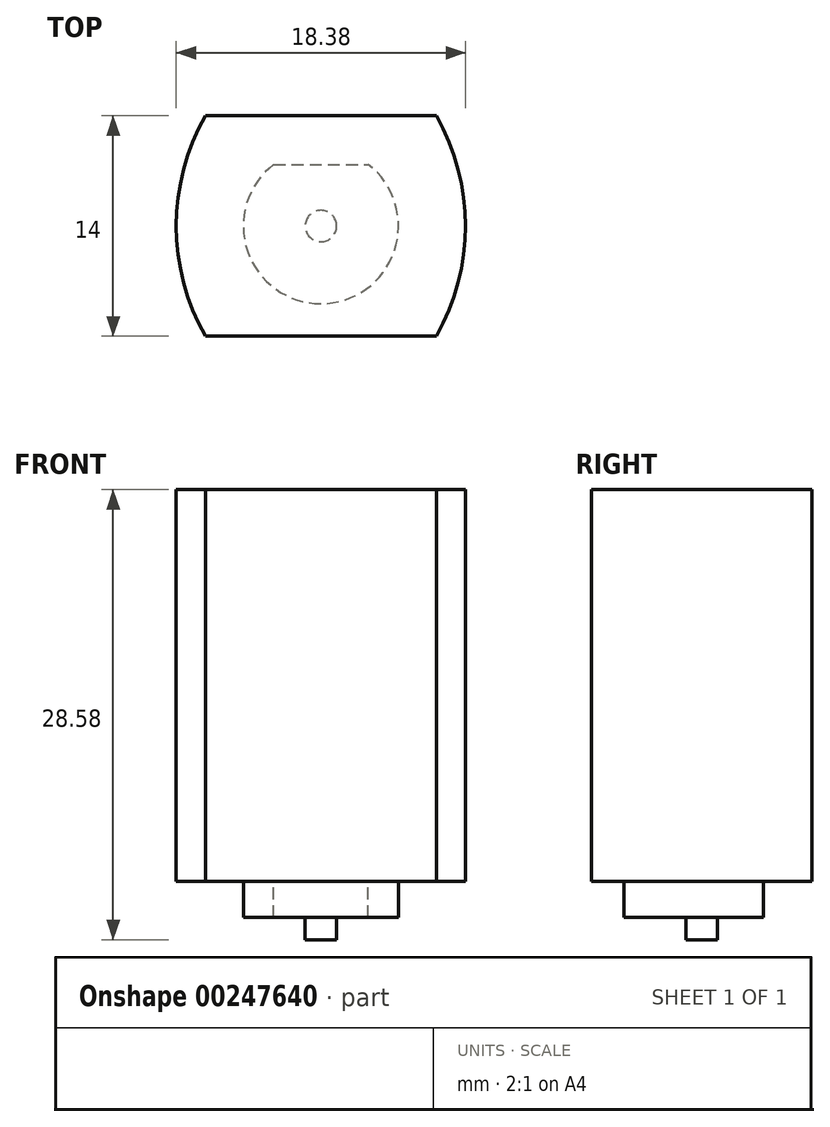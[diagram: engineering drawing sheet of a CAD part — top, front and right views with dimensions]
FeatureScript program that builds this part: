
annotation { "Feature Type Name" : "Feature", "Feature Type Description" : "" }
export const myFeature = defineFeature(function(context is Context, id is Id, definition is map)
    precondition{}
    {
        {
            var Q0;
            Q0=qCreatedBy(makeId("Top.planeOp"),FACE);
            var sketch = newSketch(context, id + "F0", { "sketchPlane" : qUnion([Q0])});
            skLineSegment(sketch, "E0.bottom", {"start": v(9.19, -7) * mm, "end": v(-9.19, -7) * mm});
            skLineSegment(sketch, "E0.top", {"start": v(9.19, 7) * mm, "end": v(-9.19, 7) * mm});
            skLineSegment(sketch, "E0.left", {"start": v(9.19, -7) * mm, "end": v(9.19, 7) * mm});
            skLineSegment(sketch, "E0.right", {"start": v(-9.19, -7) * mm, "end": v(-9.19, 7) * mm});
            skPoint(sketch, "E0.middle", {"position": v(0, 0) * mm});
            skLineSegment(sketch, "E1", {"start": v(-7.33, 7) * mm, "end": v(-7.33, -7) * mm, "construction": true});
            skLineSegment(sketch, "E2.MirrorCS", {"start": v(7.33, 7) * mm, "end": v(7.33, -7) * mm, "construction": true});
            skPoint(sketch, "E3", {"position": v(-9.19, 0) * mm});
            skArc(sketch, "E4", {"start": v(-7.33, 7) * mm, "mid": v(-9.19, 0) * mm, "end": v(-7.33, -7) * mm});
            skArc(sketch, "E5.MirrorCS", {"start": v(7.33, 7) * mm, "mid": v(9.19, 0) * mm, "end": v(7.33, -7) * mm});
            skSolve(sketch);
        }
        {
            var Q0;
            {var subQ0=sQuery(id+"F0.wireOp",EDGE,"E4");var subQ1=sQuery(id+"F0.wireOp",EDGE,"E0.bottom");var subQ2=makeQuery(id+"F0.imprint","INTERSECT",VERTEX,{"derivedFrom":[subQ1,subQ0]});Q0=makeQuery(id+"F0.imprint","IMPRINT",FACE,{"disambiguationData":[TD([[makeQuery(id+"F0.imprint","IMPRINT",EDGE,{"disambiguationData":[TD([[subQ2,1.0]])],"derivedFrom":subQ1}),-1.0]])]});}
            extrude(context, id + "F1", {"entities" : qUnion([Q0]), "depth" : 24.88 * mm, "symmetric" : true});
        }
        {
            var Q0;
            Q0=makeQuery(id+"F1.opExtrude","CAP_FACE",FACE,{"disambiguationData":[OSD([sQuery(id+"F0.wireOp",EDGE,"E0.bottom"),sQuery(id+"F0.wireOp",EDGE,"E0.top"),sQuery(id+"F0.wireOp",EDGE,"E4"),sQuery(id+"F0.wireOp",EDGE,"E5.MirrorCS")])],"isStart":true});
            var sketch = newSketch(context, id + "F2", { "sketchPlane" : qUnion([Q0])});
            skCircle(sketch, "E6", {"center": v(0, 0) * mm, "radius": 4.93 * mm});
            skLineSegment(sketch, "E7", {"start": v(0, 4.93) * mm, "end": v(0, -3.91) * mm, "construction": true});
            skLineSegment(sketch, "E8", {"start": v(-3, -3.91) * mm, "end": v(3, -3.91) * mm});
            skSolve(sketch);
        }
        {
            var Q0;
            {var subQ0=sQuery(id+"F2.wireOp",EDGE,"E8");Q0=makeQuery(id+"F2.imprint","IMPRINT",FACE,{"disambiguationData":[TD([[makeQuery(id+"F2.imprint","IMPRINT",EDGE,{"derivedFrom":subQ0}),1.0]])]});}
            extrude(context, id + "F3", {"entities" : qUnion([Q0]), "operationType" : NewBodyOperationType.ADD, "depth" : 2.28 * mm});
        }
        {
            var Q0;
            Q0=makeQuery(id+"F3.opExtrude","CAP_FACE",FACE,{"disambiguationData":[OSD([sQuery(id+"F2.wireOp",EDGE,"E6"),sQuery(id+"F2.wireOp",EDGE,"E8")])],"isStart":false});
            var sketch = newSketch(context, id + "F4", { "sketchPlane" : qUnion([Q0])});
            skCircle(sketch, "E9", {"center": v(0, 0) * mm, "radius": 1 * mm});
            skSolve(sketch);
        }
        {
            var Q0;
            Q0=makeQuery(id+"F4.imprint","IMPRINT",FACE,{"disambiguationData":[TD([[makeQuery(id+"F4.imprint","IMPRINT",EDGE,{"derivedFrom":sQuery(id+"F4.wireOp",EDGE,"E9")}),1.0]])]});
            extrude(context, id + "F5", {"entities" : qUnion([Q0]), "operationType" : NewBodyOperationType.ADD, "depth" : 1.42 * mm});
        }
    });
